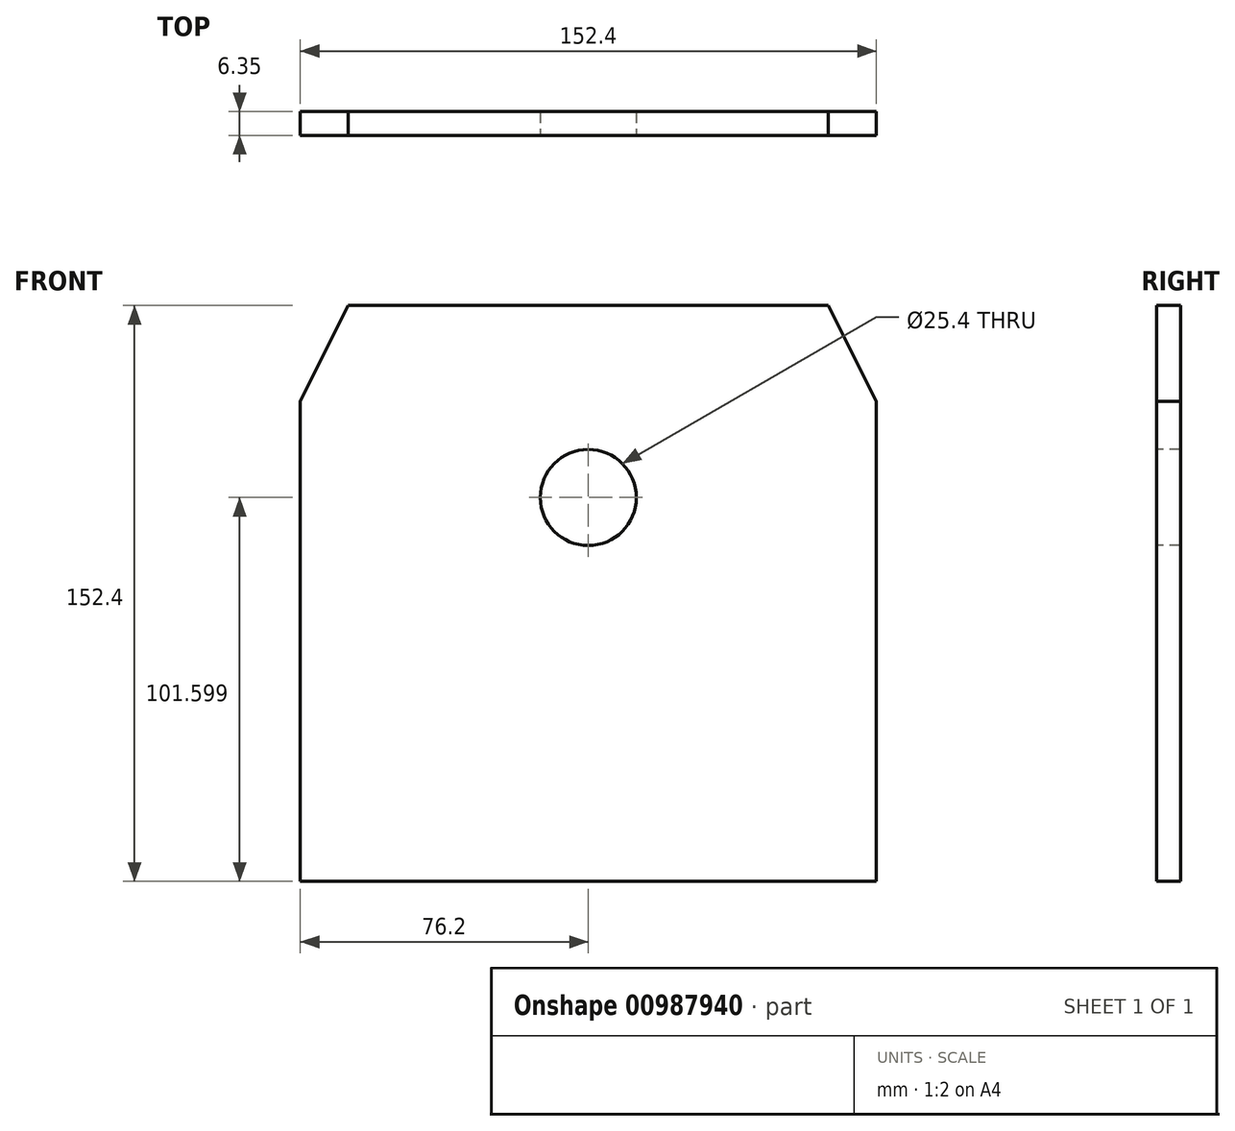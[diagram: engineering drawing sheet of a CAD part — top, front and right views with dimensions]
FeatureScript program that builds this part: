
annotation { "Feature Type Name" : "Feature", "Feature Type Description" : "" }
export const myFeature = defineFeature(function(context is Context, id is Id, definition is map)
    precondition{}
    {
        {
            var Q0;
            Q0=qCreatedBy(makeId("Front.planeOp"),FACE);
            var sketch = newSketch(context, id + "F0", { "sketchPlane" : qUnion([Q0])});
            skLineSegment(sketch, "E0.bottom", {"start": v(-175.99, 173.55) * mm, "end": v(-23.59, 173.55) * mm});
            skLineSegment(sketch, "E0.top", {"start": v(-175.99, 21.15) * mm, "end": v(-23.59, 21.15) * mm});
            skLineSegment(sketch, "E0.left", {"start": v(-175.99, 173.55) * mm, "end": v(-175.99, 21.15) * mm});
            skLineSegment(sketch, "E0.right", {"start": v(-23.59, 173.55) * mm, "end": v(-23.59, 21.15) * mm});
            skSolve(sketch);
        }
        {
            var Q0;
            Q0=makeQuery(id+"F0.imprint","IMPRINT",FACE,{"disambiguationData":[TD([[makeQuery(id+"F0.imprint","IMPRINT",EDGE,{"derivedFrom":sQuery(id+"F0.wireOp",EDGE,"E0.bottom")}),-1.0]])]});
            extrude(context, id + "F1", {"entities" : qUnion([Q0]), "depth" : 6.35 * mm, "offsetDistance" : 25.4 * mm});
        }
        {
            var Q0;
            Q0=makeQuery(id+"F1.opExtrude","CAP_FACE",FACE,{"disambiguationData":[OSD([sQuery(id+"F0.wireOp",EDGE,"E0.bottom"),sQuery(id+"F0.wireOp",EDGE,"E0.top"),sQuery(id+"F0.wireOp",EDGE,"E0.left"),sQuery(id+"F0.wireOp",EDGE,"E0.right")])],"isStart":false});
            var sketch = newSketch(context, id + "F2", { "sketchPlane" : qUnion([Q0])});
            skLineSegment(sketch, "E1", {"start": v(-175.99, 173.55) * mm, "end": v(-163.29, 173.55) * mm});
            skLineSegment(sketch, "E2", {"start": v(-163.29, 173.55) * mm, "end": v(-36.29, 173.55) * mm});
            skLineSegment(sketch, "E3", {"start": v(-36.29, 173.55) * mm, "end": v(-23.59, 173.55) * mm});
            skLineSegment(sketch, "E4", {"start": v(-23.59, 173.55) * mm, "end": v(-23.59, 148.15) * mm});
            skLineSegment(sketch, "E5", {"start": v(-23.59, 148.15) * mm, "end": v(-175.99, 148.15) * mm});
            skLineSegment(sketch, "E6", {"start": v(-175.99, 148.15) * mm, "end": v(-175.99, 173.55) * mm});
            skLineSegment(sketch, "E7", {"start": v(-163.29, 173.55) * mm, "end": v(-175.99, 148.15) * mm});
            skLineSegment(sketch, "E8", {"start": v(-36.29, 173.55) * mm, "end": v(-23.59, 148.15) * mm});
            skSolve(sketch);
        }
        {
            var Q0;
            Q0=makeQuery(id+"F2.imprint","IMPRINT",FACE,{"disambiguationData":[TD([[makeQuery(id+"F2.imprint","IMPRINT",EDGE,{"derivedFrom":sQuery(id+"F2.wireOp",EDGE,"E1")}),-1.0]])]});
            var Q1;
            Q1=makeQuery(id+"F2.imprint","IMPRINT",FACE,{"disambiguationData":[TD([[makeQuery(id+"F2.imprint","IMPRINT",EDGE,{"derivedFrom":sQuery(id+"F2.wireOp",EDGE,"E3")}),-1.0]])]});
            extrude(context, id + "F3", {"entities" : qUnion([Q0, Q1]), "operationType" : NewBodyOperationType.REMOVE, "oppositeDirection" : true, "depth" : 25.4 * mm, "offsetDistance" : 25.4 * mm});
        }
        {
            var Q0;
            Q0=makeQuery(id+"F1.opExtrude","CAP_FACE",FACE,{"disambiguationData":[OSD([sQuery(id+"F0.wireOp",EDGE,"E0.bottom"),sQuery(id+"F0.wireOp",EDGE,"E0.top"),sQuery(id+"F0.wireOp",EDGE,"E0.left"),sQuery(id+"F0.wireOp",EDGE,"E0.right")])],"isStart":false});
            var sketch = newSketch(context, id + "F4", { "sketchPlane" : qUnion([Q0])});
            skLineSegment(sketch, "E9", {"start": v(-99.79, 173.55) * mm, "end": v(-99.79, 122.75) * mm});
            skCircle(sketch, "E10", {"center": v(-99.79, 122.75) * mm, "radius": 12.7 * mm});
            skLineSegment(sketch, "E11.bottom", {"start": v(-175.99, 21.15) * mm, "end": v(-23.59, 21.15) * mm});
            skLineSegment(sketch, "E11.top", {"start": v(-175.99, 71.95) * mm, "end": v(-23.59, 71.95) * mm});
            skLineSegment(sketch, "E11.left", {"start": v(-175.99, 21.15) * mm, "end": v(-175.99, 71.95) * mm});
            skLineSegment(sketch, "E11.right", {"start": v(-23.59, 21.15) * mm, "end": v(-23.59, 71.95) * mm});
            skSolve(sketch);
        }
        {
            var Q0;
            Q0=makeQuery(id+"F4.imprint","IMPRINT",FACE,{"disambiguationData":[TD([[makeQuery(id+"F4.imprint","IMPRINT",EDGE,{"derivedFrom":sQuery(id+"F4.wireOp",EDGE,"E10")}),1.0]])]});
            extrude(context, id + "F5", {"entities" : qUnion([Q0]), "operationType" : NewBodyOperationType.REMOVE, "oppositeDirection" : true, "depth" : 25.4 * mm, "offsetDistance" : 25.4 * mm});
        }
    });
